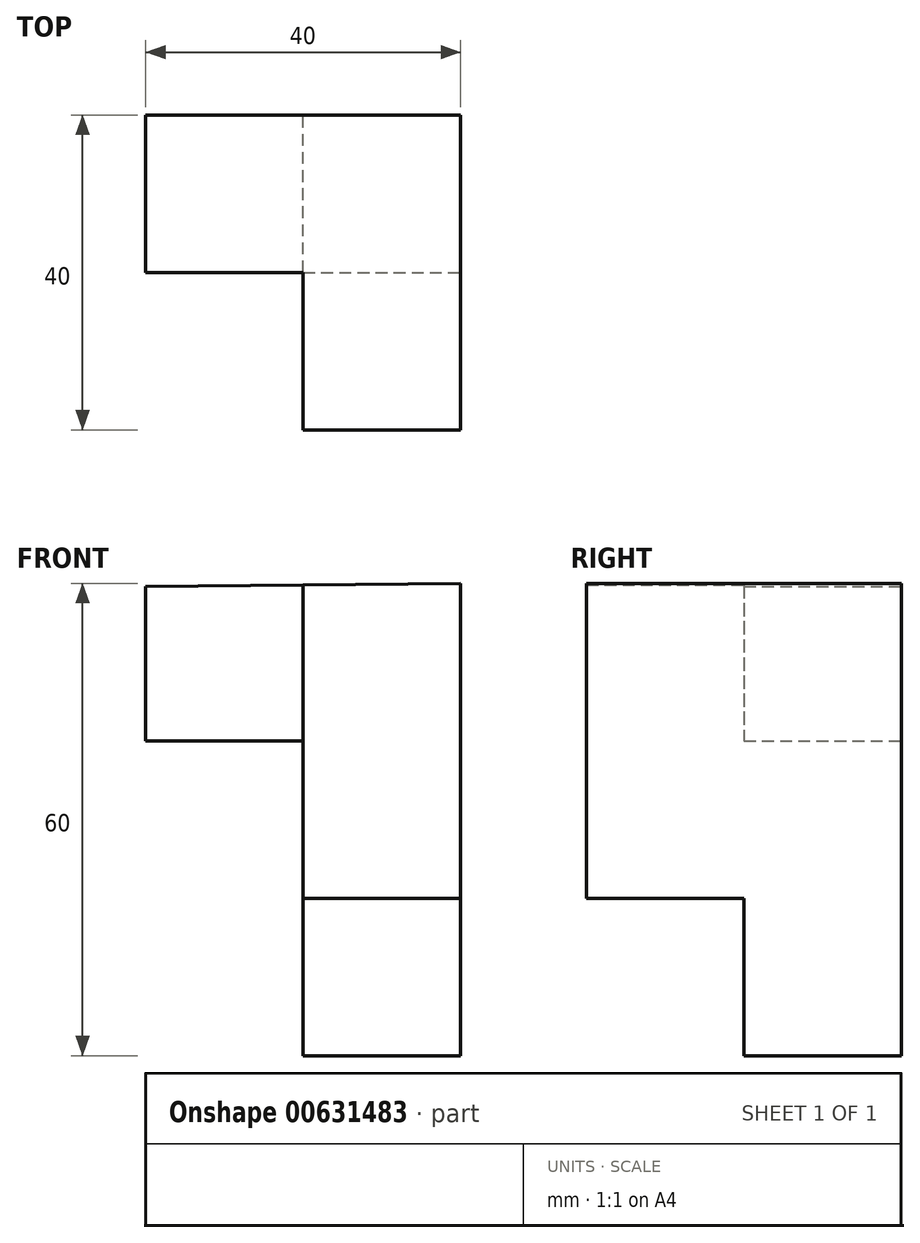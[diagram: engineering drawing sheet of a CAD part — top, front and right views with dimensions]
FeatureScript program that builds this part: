
annotation { "Feature Type Name" : "Feature", "Feature Type Description" : "" }
export const myFeature = defineFeature(function(context is Context, id is Id, definition is map)
    precondition{}
    {
        {
            var Q0;
            Q0=qCreatedBy(makeId("Front.planeOp"),FACE);
            var sketch = newSketch(context, id + "F0", { "sketchPlane" : qUnion([Q0])});
            skLineSegment(sketch, "E0", {"start": v(-17.75, 24.23) * mm, "end": v(-17.75, 4.63) * mm});
            skLineSegment(sketch, "E1", {"start": v(-17.75, 4.63) * mm, "end": v(2.25, 4.63) * mm});
            skLineSegment(sketch, "E2", {"start": v(2.25, 4.63) * mm, "end": v(2.25, -35.37) * mm});
            skLineSegment(sketch, "E3", {"start": v(2.25, -35.37) * mm, "end": v(22.25, -35.37) * mm});
            skLineSegment(sketch, "E4", {"start": v(22.25, -35.37) * mm, "end": v(22.25, 24.63) * mm});
            skLineSegment(sketch, "E5", {"start": v(22.25, 24.63) * mm, "end": v(-17.75, 24.23) * mm});
            skSolve(sketch);
        }
        {
            var Q0;
            Q0=makeQuery(id+"F0.imprint","IMPRINT",FACE,{"disambiguationData":[TD([[makeQuery(id+"F0.imprint","IMPRINT",EDGE,{"derivedFrom":sQuery(id+"F0.wireOp",EDGE,"E0")}),1.0]])]});
            extrude(context, id + "F1", {"entities" : qUnion([Q0]), "depth" : 20 * mm, "offsetDistance" : 25 * mm});
        }
        {
            var Q0;
            Q0=makeQuery(id+"F1.opExtrude","CAP_FACE",FACE,{"disambiguationData":[OSD([sQuery(id+"F0.wireOp",EDGE,"E0"),sQuery(id+"F0.wireOp",EDGE,"E1"),sQuery(id+"F0.wireOp",EDGE,"E2"),sQuery(id+"F0.wireOp",EDGE,"E3"),sQuery(id+"F0.wireOp",EDGE,"E4"),sQuery(id+"F0.wireOp",EDGE,"E5")])],"isStart":false});
            var sketch = newSketch(context, id + "F2", { "sketchPlane" : qUnion([Q0])});
            skLineSegment(sketch, "E6", {"start": v(2.25, 24.43) * mm, "end": v(2.25, -15.37) * mm});
            skLineSegment(sketch, "E7", {"start": v(2.25, -15.37) * mm, "end": v(22.25, -15.37) * mm});
            skLineSegment(sketch, "E8", {"start": v(22.25, -15.37) * mm, "end": v(22.25, 24.63) * mm});
            skLineSegment(sketch, "E9", {"start": v(22.25, 24.63) * mm, "end": v(2.25, 24.43) * mm});
            skSolve(sketch);
        }
        {
            var Q0;
            {var subQ0=sQuery(id+"F2.wireOp",EDGE,"E7");Q0=makeQuery(id+"F2.imprint","IMPRINT",FACE,{"disambiguationData":[TD([[makeQuery(id+"F2.imprint","IMPRINT",EDGE,{"derivedFrom":subQ0}),1.0]])]});}
            extrude(context, id + "F3", {"entities" : qUnion([Q0]), "operationType" : NewBodyOperationType.ADD, "depth" : 20 * mm, "offsetDistance" : 25 * mm});
        }
    });
